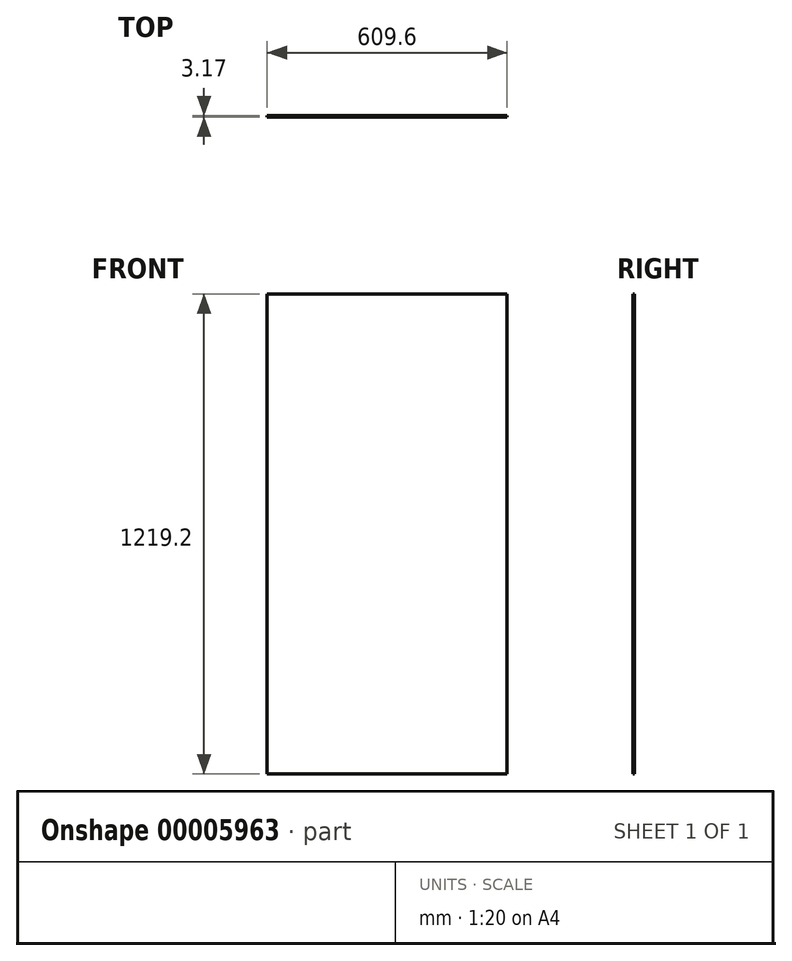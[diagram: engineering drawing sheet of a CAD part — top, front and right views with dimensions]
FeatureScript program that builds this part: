
annotation { "Feature Type Name" : "Feature", "Feature Type Description" : "" }
export const myFeature = defineFeature(function(context is Context, id is Id, definition is map)
    precondition{}
    {
        {
            var Q0;
            Q0=qCreatedBy(makeId("Front.planeOp"),FACE);
            var sketch = newSketch(context, id + "F0", { "sketchPlane" : qUnion([Q0])});
            skLineSegment(sketch, "E0.bottom", {"start": v(-424.22, 536.33) * mm, "end": v(185.38, 536.33) * mm});
            skLineSegment(sketch, "E0.top", {"start": v(-424.22, -682.87) * mm, "end": v(185.38, -682.87) * mm});
            skLineSegment(sketch, "E0.left", {"start": v(-424.22, 536.33) * mm, "end": v(-424.22, -682.87) * mm});
            skLineSegment(sketch, "E0.right", {"start": v(185.38, 536.33) * mm, "end": v(185.38, -682.87) * mm});
            skSolve(sketch);
        }
        {
            var Q0;
            Q0=qSketchRegion(id+"F0",true);
            extrude(context, id + "F1", {"entities" : qUnion([Q0]), "depth" : 3.17 * mm});
        }
    });
